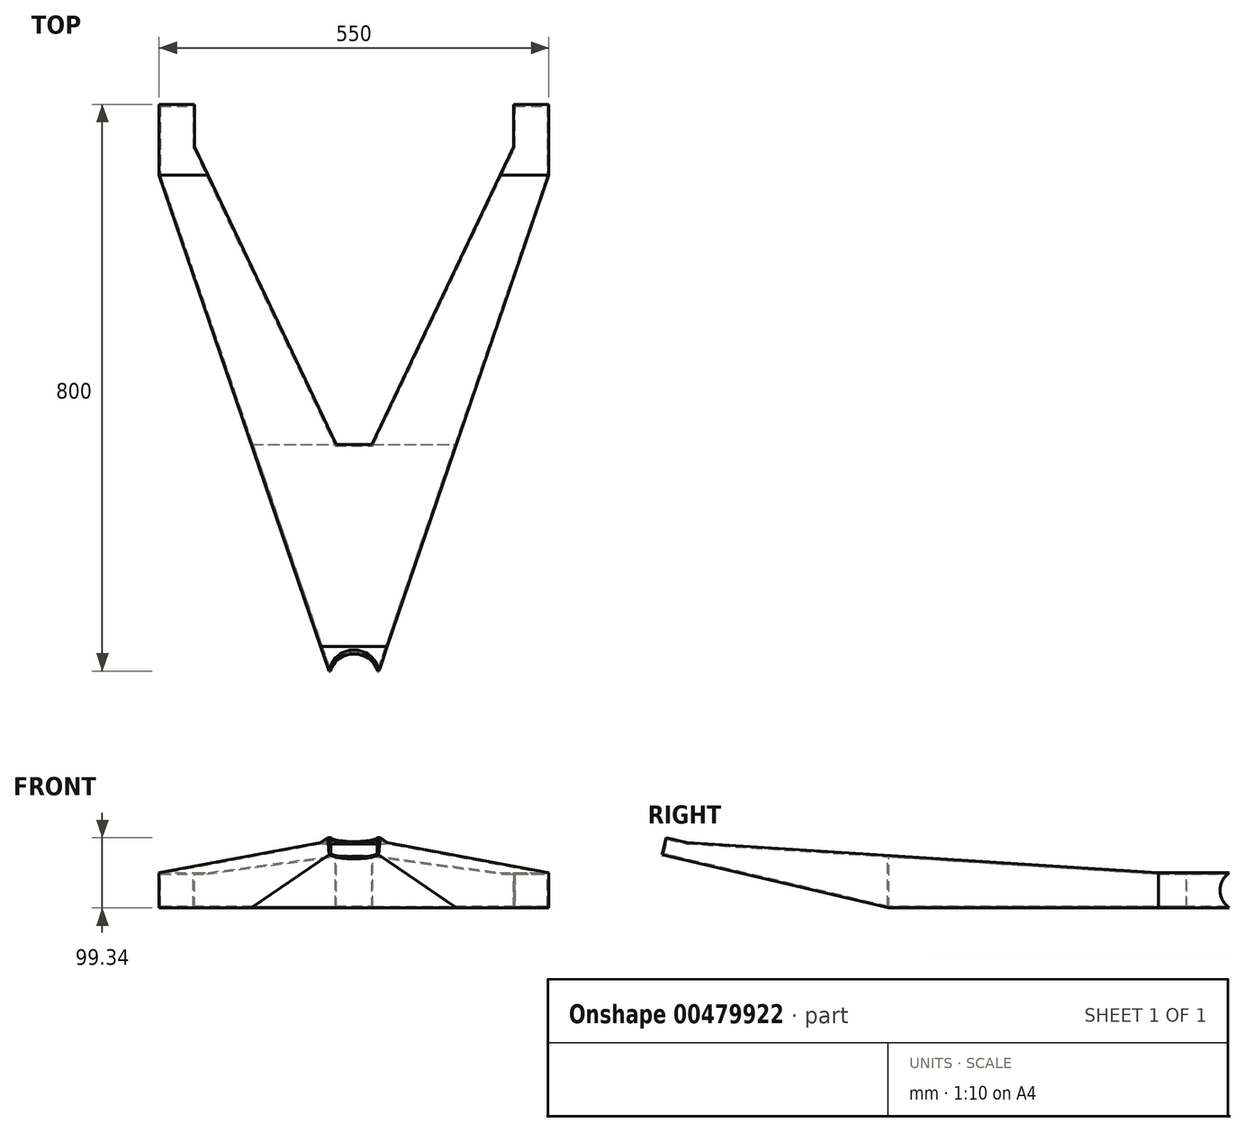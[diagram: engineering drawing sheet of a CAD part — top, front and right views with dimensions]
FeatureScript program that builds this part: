
annotation { "Feature Type Name" : "Feature", "Feature Type Description" : "" }
export const myFeature = defineFeature(function(context is Context, id is Id, definition is map)
    precondition{}
    {
        {
            var Q0;
            Q0=qCreatedBy(makeId("Top.planeOp"),FACE);
            var sketch = newSketch(context, id + "F0", { "sketchPlane" : qUnion([Q0])});
            skLineSegment(sketch, "E0.bottom", {"start": v(-275, 576.85) * mm, "end": v(-225, 576.85) * mm});
            skLineSegment(sketch, "E0.left", {"start": v(-275, 576.85) * mm, "end": v(-275, 476.85) * mm});
            skLineSegment(sketch, "E0.right", {"start": v(275, 576.85) * mm, "end": v(275, 476.85) * mm});
            skLineSegment(sketch, "E1", {"start": v(-225, 576.85) * mm, "end": v(-225, 516.85) * mm});
            skLineSegment(sketch, "E2", {"start": v(-225, 516.85) * mm, "end": v(-25, 96.85) * mm});
            skLineSegment(sketch, "E3", {"start": v(-25, 96.85) * mm, "end": v(25, 96.85) * mm});
            skLineSegment(sketch, "E4", {"start": v(25, 96.85) * mm, "end": v(225, 516.85) * mm});
            skLineSegment(sketch, "E5", {"start": v(225, 516.85) * mm, "end": v(225, 576.85) * mm});
            skLineSegment(sketch, "E6", {"start": v(275, 476.85) * mm, "end": v(35, -223.15) * mm});
            skLineSegment(sketch, "E7", {"start": v(-35, -223.15) * mm, "end": v(-275, 476.85) * mm});
            skLineSegment(sketch, "E8.trimOffspring", {"start": v(225, 576.85) * mm, "end": v(275, 576.85) * mm});
            skLineSegment(sketch, "E9", {"start": v(-35, -223.15) * mm, "end": v(35, -223.15) * mm});
            skPoint(sketch, "E10", {"position": v(0, -223.15) * mm});
            skPoint(sketch, "E11", {"position": v(0, 96.85) * mm});
            skSolve(sketch);
        }
        {
            var Q0;
            Q0=makeQuery(id+"F0.imprint","IMPRINT",FACE,{"disambiguationData":[TD([[makeQuery(id+"F0.imprint","IMPRINT",EDGE,{"derivedFrom":sQuery(id+"F0.wireOp",EDGE,"E0.bottom")}),-1.0]])]});
            extrude(context, id + "F1", {"entities" : qUnion([Q0]), "oppositeDirection" : true, "depth" : 150 * mm});
        }
        {
            var Q0;
            Q0=makeQuery(id+"F1.opExtrude","SWEPT_FACE",FACE,{"disambiguationData":[OSD([sQuery(id+"F0.wireOp",EDGE,"E0.right")])]});
            var sketch = newSketch(context, id + "F2", { "sketchPlane" : qUnion([Q0])});
            skLineSegment(sketch, "E12.0.0", {"start": v(476.85, 0) * mm, "end": v(-223.15, 0) * mm});
            skLineSegment(sketch, "E12.0.1", {"start": v(-223.15, 0) * mm, "end": v(-223.15, -150) * mm});
            skLineSegment(sketch, "E12.0.2", {"start": v(-223.15, -150) * mm, "end": v(476.85, -150) * mm});
            skLineSegment(sketch, "E12.0.3", {"start": v(476.85, -150) * mm, "end": v(476.85, 0) * mm});
            skLineSegment(sketch, "E13.0.0", {"start": v(576.85, 0) * mm, "end": v(476.85, 0) * mm});
            skLineSegment(sketch, "E13.0.1", {"start": v(476.85, 0) * mm, "end": v(476.85, -150) * mm});
            skLineSegment(sketch, "E13.0.2", {"start": v(476.85, -150) * mm, "end": v(576.85, -150) * mm});
            skLineSegment(sketch, "E13.0.3", {"start": v(576.85, -150) * mm, "end": v(576.85, 0) * mm});
            skLineSegment(sketch, "E14", {"start": v(576.85, -150) * mm, "end": v(96.85, -150) * mm});
            skLineSegment(sketch, "E15", {"start": v(96.85, -150) * mm, "end": v(-223.15, -75) * mm});
            skLineSegment(sketch, "E16", {"start": v(-223.15, -75) * mm, "end": v(-217.45, -50.66) * mm});
            skLineSegment(sketch, "E17", {"start": v(-217.45, -50.66) * mm, "end": v(-188.24, -57.5) * mm});
            skLineSegment(sketch, "E18", {"start": v(-188.24, -57.5) * mm, "end": v(476.85, -100) * mm});
            skLineSegment(sketch, "E19", {"start": v(476.85, -100) * mm, "end": v(576.85, -100) * mm});
            skSolve(sketch);
        }
        {
            var Q0;
            {var subQ3=sQuery(id+"F2.wireOp",EDGE,"E15");Q0=makeQuery(id+"F2.imprint","IMPRINT",FACE,{"disambiguationData":[TD([[makeQuery(id+"F2.imprint","IMPRINT",EDGE,{"derivedFrom":subQ3}),1.0]])]});}
            var Q1;
            {var subQ2=sQuery(id+"F2.wireOp",EDGE,"E12.0.0");Q1=makeQuery(id+"F2.imprint","IMPRINT",FACE,{"disambiguationData":[TD([[makeQuery(id+"F2.imprint","IMPRINT",EDGE,{"derivedFrom":subQ2}),1.0]])]});}
            var Q2;
            {var subQ0=sQuery(id+"F2.wireOp",EDGE,"E13.0.0");Q2=makeQuery(id+"F2.imprint","IMPRINT",FACE,{"disambiguationData":[TD([[makeQuery(id+"F2.imprint","IMPRINT",EDGE,{"derivedFrom":subQ0}),1.0]])]});}
            extrude(context, id + "F3", {"entities" : qUnion([Q0, Q1, Q2]), "operationType" : NewBodyOperationType.REMOVE, "endBound" : BoundingType.THROUGH_ALL, "oppositeDirection" : true, "depth" : 25 * mm});
        }
        {
            var Q0;
            Q0=makeQuery(id+"F3.boolean.opBoolean","COPY",FACE,{"derivedFrom":makeQuery(id+"F3.opExtrude","SWEPT_FACE",FACE,{"disambiguationData":[OSD([sQuery(id+"F2.wireOp",EDGE,"E17")])]})});
            var sketch = newSketch(context, id + "F4", { "sketchPlane" : qUnion([Q0])});
            skLineSegment(sketch, "E20.0.0", {"start": v(46.97, -170.15) * mm, "end": v(-46.97, -170.15) * mm});
            skLineSegment(sketch, "E20.0.1", {"start": v(-46.97, -170.15) * mm, "end": v(-36.96, -200.15) * mm});
            skLineSegment(sketch, "E20.0.2", {"start": v(-36.96, -200.15) * mm, "end": v(36.96, -200.15) * mm});
            skLineSegment(sketch, "E20.0.3", {"start": v(36.96, -200.15) * mm, "end": v(46.97, -170.15) * mm});
            skLineSegment(sketch, "E21", {"start": v(0, -200.15) * mm, "end": v(0, -210.15) * mm});
            skPoint(sketch, "E21.endSnap0", {"position": v(0, -200.15) * mm});
            skCircle(sketch, "E22", {"center": v(0, -210.15) * mm, "radius": 35 * mm});
            skSolve(sketch);
        }
        {
            var Q0;
            {var subQ0=sQuery(id+"F4.wireOp",EDGE,"E20.0.2");var subQ1=makeQuery(id+"F4.imprint","IMPRINT",VERTEX,{"derivedFrom":subQ0});Q0=makeQuery(id+"F4.imprint","IMPRINT",FACE,{"disambiguationData":[TD([[makeQuery(id+"F4.imprint","IMPRINT",EDGE,{"disambiguationData":[TD([[subQ1,1.0]])],"derivedFrom":subQ0}),1.0]])]});}
            extrude(context, id + "F5", {"entities" : qUnion([Q0]), "operationType" : NewBodyOperationType.REMOVE, "endBound" : BoundingType.THROUGH_ALL, "oppositeDirection" : true, "depth" : 25 * mm});
        }
        {
            var Q0;
            Q0=makeQuery(id+"F1.opExtrude","SWEPT_FACE",FACE,{"disambiguationData":[OSD([sQuery(id+"F0.wireOp",EDGE,"E0.right")])]});
            var sketch = newSketch(context, id + "F6", { "sketchPlane" : qUnion([Q0])});
            skLineSegment(sketch, "E23.0.0", {"start": v(576.85, -100) * mm, "end": v(476.85, -100) * mm});
            skLineSegment(sketch, "E23.0.1", {"start": v(476.85, -100) * mm, "end": v(476.85, -150) * mm});
            skLineSegment(sketch, "E23.0.2", {"start": v(476.85, -150) * mm, "end": v(576.85, -150) * mm});
            skLineSegment(sketch, "E23.0.3", {"start": v(576.85, -150) * mm, "end": v(576.85, -100) * mm});
            skLineSegment(sketch, "E24", {"start": v(576.85, -125) * mm, "end": v(593.85, -125) * mm});
            skCircle(sketch, "E25", {"center": v(593.85, -125) * mm, "radius": 30 * mm});
            skSolve(sketch);
        }
        {
            var Q0;
            {var subQ0=sQuery(id+"F6.wireOp",EDGE,"E23.0.3");var subQ1=makeQuery(id+"F6.imprint","IMPRINT",VERTEX,{"derivedFrom":subQ0});Q0=makeQuery(id+"F6.imprint","IMPRINT",FACE,{"disambiguationData":[TD([[makeQuery(id+"F6.imprint","IMPRINT",EDGE,{"disambiguationData":[TD([[subQ1,1.0]])],"derivedFrom":subQ0}),1.0]])]});}
            extrude(context, id + "F7", {"entities" : qUnion([Q0]), "operationType" : NewBodyOperationType.REMOVE, "endBound" : BoundingType.THROUGH_ALL, "oppositeDirection" : true, "depth" : 25 * mm});
        }
        {
            var Q0;
            Q0=makeQuery(id+"F7.boolean.opBoolean","COPY",FACE,{"disambiguationData":[TD([makeQuery(id+"F1.opExtrude","SWEPT_FACE",FACE,{"disambiguationData":[OSD([sQuery(id+"F0.wireOp",EDGE,"E0.right")])]})])],"derivedFrom":makeQuery(id+"F7.opExtrude","SWEPT_FACE",FACE,{"disambiguationData":[OSD([sQuery(id+"F6.wireOp",EDGE,"E25")])]})});
            var Q1;
            Q1=makeQuery(id+"F7.boolean.opBoolean","COPY",FACE,{"disambiguationData":[TD([makeQuery(id+"F1.opExtrude","SWEPT_FACE",FACE,{"disambiguationData":[OSD([sQuery(id+"F0.wireOp",EDGE,"E0.bottom")])]})])],"derivedFrom":makeQuery(id+"F7.opExtrude","SWEPT_FACE",FACE,{"disambiguationData":[OSD([sQuery(id+"F6.wireOp",EDGE,"E25")])]})});
            var Q2;
            Q2=makeQuery(id+"F5.boolean.opBoolean","COPY",FACE,{"derivedFrom":makeQuery(id+"F5.opExtrude","SWEPT_FACE",FACE,{"disambiguationData":[OSD([sQuery(id+"F4.wireOp",EDGE,"E22")])]})});
            shell(context, id + "F8", {"entities" : qUnion([Q0, Q1, Q2]), "thickness" : 2 * mm});
        }
    });
